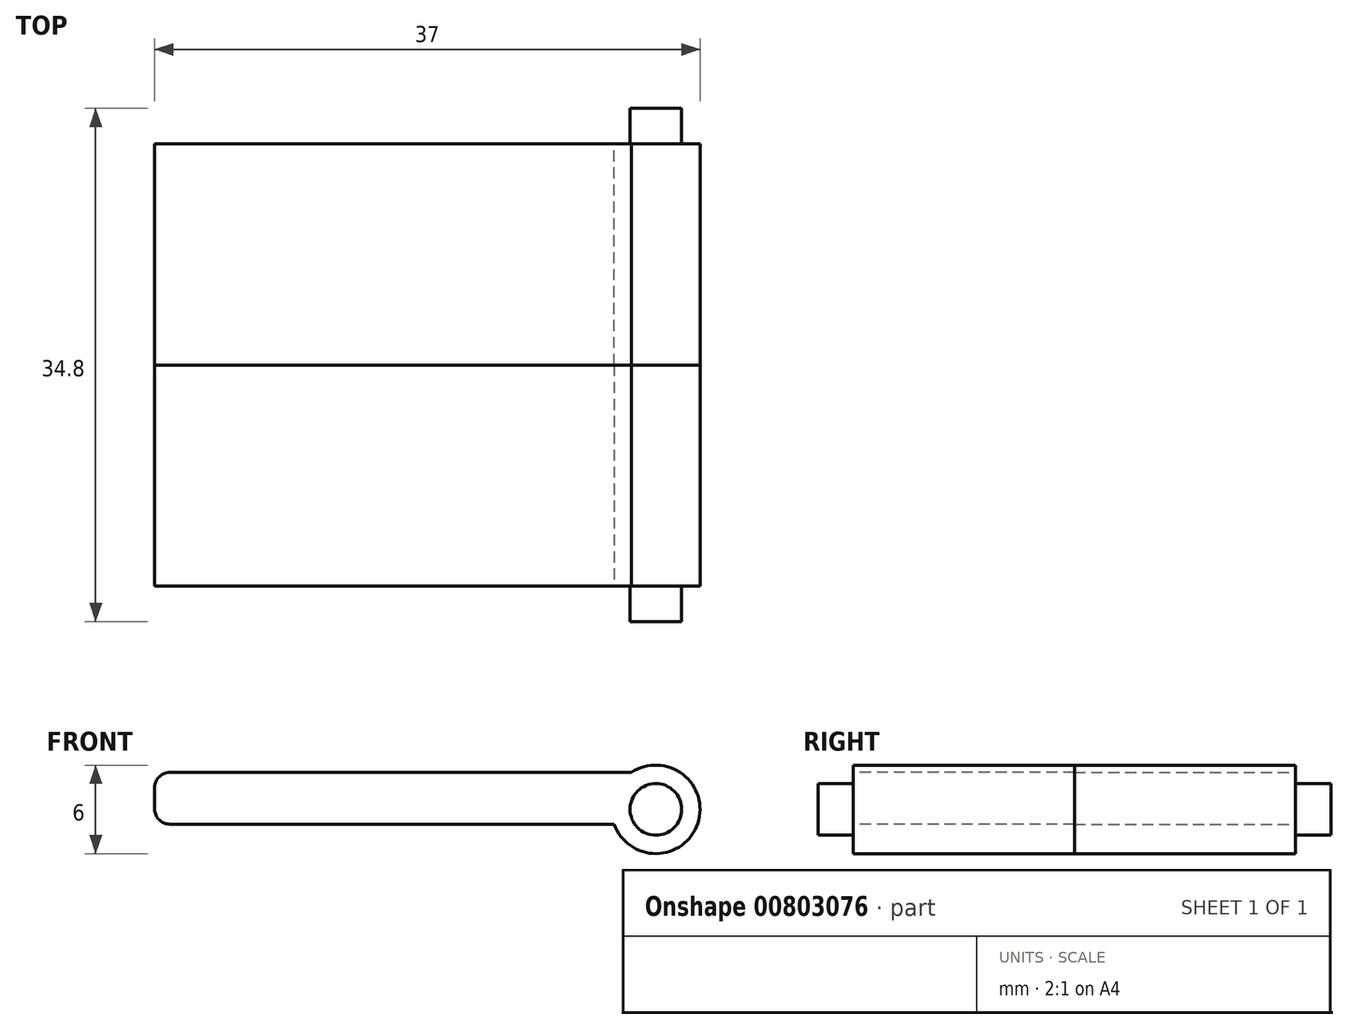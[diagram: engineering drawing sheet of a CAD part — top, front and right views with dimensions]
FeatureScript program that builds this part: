
annotation { "Feature Type Name" : "Feature", "Feature Type Description" : "" }
export const myFeature = defineFeature(function(context is Context, id is Id, definition is map)
    precondition{}
    {
        {
            var Q0;
            Q0=qCreatedBy(makeId("Front.planeOp"),FACE);
            var sketch = newSketch(context, id + "F0", { "sketchPlane" : qUnion([Q0])});
            skLineSegment(sketch, "E0", {"start": v(0, 0) * mm, "end": v(-22.58, 0) * mm, "construction": true});
            skLineSegment(sketch, "E1", {"start": v(0, 12.55) * mm, "end": v(0, -13.37) * mm, "construction": true});
            skLineSegment(sketch, "E2.left", {"start": v(0, 0) * mm, "end": v(0, 3.5) * mm});
            skCircle(sketch, "E3", {"center": v(0, 0) * mm, "radius": 3 * mm});
            skCircle(sketch, "E4", {"center": v(0, 0) * mm, "radius": 1.75 * mm});
            skLineSegment(sketch, "E5.bottom", {"start": v(-33, 2.5) * mm, "end": v(0, 2.5) * mm});
            skLineSegment(sketch, "E5.top", {"start": v(-33, -1) * mm, "end": v(0, -1) * mm});
            skLineSegment(sketch, "E5.left", {"start": v(-34, 1.5) * mm, "end": v(-34, 0) * mm});
            skLineSegment(sketch, "E5.right", {"start": v(0, 2.5) * mm, "end": v(0, -1) * mm});
            skPoint(sketch, "E6.visualSharp", {"position": v(-34, 2.5) * mm});
            skArc(sketch, "E6.filletArc", {"start": v(-33, 2.5) * mm, "mid": v(-33.7, 2.2) * mm, "end": v(-34, 1.5) * mm});
            skPoint(sketch, "E7.visualSharp", {"position": v(-34, -1) * mm});
            skArc(sketch, "E7.filletArc", {"start": v(-34, 0) * mm, "mid": v(-33.7, -0.7) * mm, "end": v(-33, -1) * mm});
            skSolve(sketch);
        }
        {
            var Q0;
            {var subQ3=sQuery(id+"F0.wireOp",EDGE,"E5.right");var subQ6=makeQuery(id+"F0.imprint","IMPRINT",VERTEX,{"derivedFrom":subQ3});Q0=makeQuery(id+"F0.imprint","IMPRINT",FACE,{"disambiguationData":[TD([[makeQuery(id+"F0.imprint","IMPRINT",EDGE,{"disambiguationData":[TD([[subQ6,1.0]])],"derivedFrom":subQ3}),-1.0]])]});}
            var Q1;
            {var subQ3=sQuery(id+"F0.wireOp",EDGE,"E5.right");var subQ6=makeQuery(id+"F0.imprint","IMPRINT",VERTEX,{"derivedFrom":subQ3});Q1=makeQuery(id+"F0.imprint","IMPRINT",FACE,{"disambiguationData":[TD([[makeQuery(id+"F0.imprint","IMPRINT",EDGE,{"disambiguationData":[TD([[subQ6,1.0]])],"derivedFrom":subQ3}),1.0]])]});}
            extrude(context, id + "F1", {"entities" : qUnion([Q0, Q1]), "depth" : 2.4 * mm, "offsetDistance" : 25 * mm});
        }
        {
            var Q0;
            {var subQ5=sQuery(id+"F0.wireOp",EDGE,"E5.left");Q0=makeQuery(id+"F0.imprint","IMPRINT",FACE,{"disambiguationData":[TD([[makeQuery(id+"F0.imprint","IMPRINT",EDGE,{"derivedFrom":subQ5}),1.0]])]});}
            var Q1;
            {var subQ3=sQuery(id+"F0.wireOp",EDGE,"E5.right");var subQ6=makeQuery(id+"F0.imprint","IMPRINT",VERTEX,{"derivedFrom":subQ3});Q1=makeQuery(id+"F0.imprint","IMPRINT",FACE,{"disambiguationData":[TD([[makeQuery(id+"F0.imprint","IMPRINT",EDGE,{"disambiguationData":[TD([[subQ6,1.0]])],"derivedFrom":subQ3}),-1.0]])]});}
            var Q2;
            {var subQ3=sQuery(id+"F0.wireOp",EDGE,"E5.right");var subQ6=makeQuery(id+"F0.imprint","IMPRINT",VERTEX,{"derivedFrom":subQ3});Q2=makeQuery(id+"F0.imprint","IMPRINT",FACE,{"disambiguationData":[TD([[makeQuery(id+"F0.imprint","IMPRINT",EDGE,{"disambiguationData":[TD([[subQ6,1.0]])],"derivedFrom":subQ3}),1.0]])]});}
            var Q3;
            {var subQ1=sQuery(id+"F0.wireOp",EDGE,"E3");var subQ7=sQuery(id+"F0.wireOp",EDGE,"E5.bottom");var subQ9=makeQuery(id+"F0.imprint","INTERSECT",VERTEX,{"derivedFrom":[subQ1,subQ7]});Q3=makeQuery(id+"F0.imprint","IMPRINT",FACE,{"disambiguationData":[TD([[makeQuery(id+"F0.imprint","IMPRINT",EDGE,{"disambiguationData":[TD([[subQ9,-1.0]])],"derivedFrom":subQ1}),1.0]])]});}
            var Q4;
            {var subQ1=sQuery(id+"F0.wireOp",EDGE,"E2.left");var subQ3=sQuery(id+"F0.wireOp",EDGE,"E3");var subQ4=makeQuery(id+"F0.imprint","INTERSECT",VERTEX,{"derivedFrom":[subQ1,subQ3]});Q4=makeQuery(id+"F0.imprint","IMPRINT",FACE,{"disambiguationData":[TD([[makeQuery(id+"F0.imprint","IMPRINT",EDGE,{"disambiguationData":[TD([[subQ4,-1.0]])],"derivedFrom":subQ3}),1.0]])]});}
            var Q5;
            {var subQ1=sQuery(id+"F0.wireOp",EDGE,"E3");var subQ5=sQuery(id+"F0.wireOp",EDGE,"E2.left");var subQ6=makeQuery(id+"F0.imprint","INTERSECT",VERTEX,{"derivedFrom":[subQ5,subQ1]});Q5=makeQuery(id+"F0.imprint","IMPRINT",FACE,{"disambiguationData":[TD([[makeQuery(id+"F0.imprint","IMPRINT",EDGE,{"disambiguationData":[TD([[subQ6,1.0]])],"derivedFrom":subQ1}),1.0]])]});}
            extrude(context, id + "F2", {"entities" : qUnion([Q0, Q1, Q2, Q3, Q4, Q5]), "operationType" : NewBodyOperationType.ADD, "oppositeDirection" : true, "depth" : 15 * mm, "offsetDistance" : 25 * mm});
        }
        {
            var Q0;
            Q0=makeQuery(id+"F1.opExtrude","SWEPT_BODY",BODY,{"disambiguationData":[OSD([sQuery(id+"F0.wireOp",EDGE,"E4")])]});
            var Q1;
            Q1=makeQuery(id+"F2.opExtrude","CAP_FACE",FACE,{"disambiguationData":[OSD([sQuery(id+"F0.wireOp",EDGE,"E3"),sQuery(id+"F0.wireOp",EDGE,"E5.bottom"),sQuery(id+"F0.wireOp",EDGE,"E5.top"),sQuery(id+"F0.wireOp",EDGE,"E5.left")])],"isStart":false});
            mirror(context, id + "F3", {"entities" : qUnion([Q0]), "mirrorPlane" : qUnion([Q1])});
        }
    });
